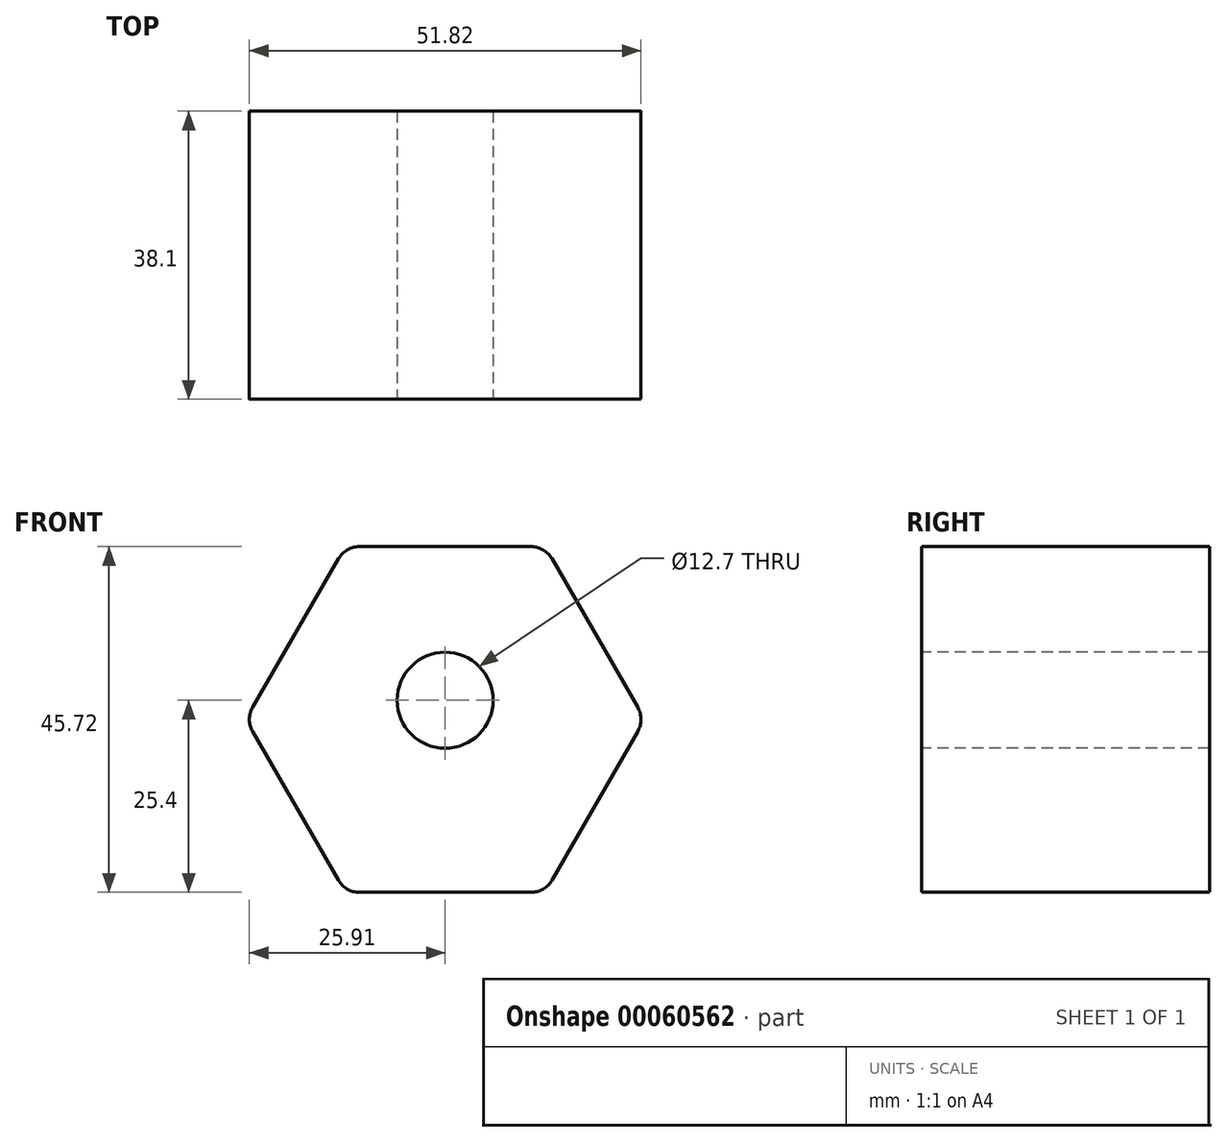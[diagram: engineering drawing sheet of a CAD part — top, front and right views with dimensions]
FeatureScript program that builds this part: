
annotation { "Feature Type Name" : "Feature", "Feature Type Description" : "" }
export const myFeature = defineFeature(function(context is Context, id is Id, definition is map)
    precondition{}
    {
        {
            var Q0;
            Q0=qCreatedBy(makeId("Front.planeOp"),FACE);
            var sketch = newSketch(context, id + "F0", { "sketchPlane" : qUnion([Q0])});
            skCircle(sketch, "E0.cCircle", {"center": v(0, 0) * mm, "radius": 22.86 * mm, "construction": true});
            skLineSegment(sketch, "E0.0", {"start": v(-13.2, 22.86) * mm, "end": v(13.2, 22.86) * mm});
            skLineSegment(sketch, "E0.1", {"start": v(13.2, 22.86) * mm, "end": v(26.4, 0) * mm});
            skLineSegment(sketch, "E0.2", {"start": v(26.4, 0) * mm, "end": v(13.2, -22.86) * mm});
            skLineSegment(sketch, "E0.3", {"start": v(13.2, -22.86) * mm, "end": v(-13.2, -22.86) * mm});
            skLineSegment(sketch, "E0.4", {"start": v(-13.2, -22.86) * mm, "end": v(-26.4, 0) * mm});
            skLineSegment(sketch, "E0.5", {"start": v(-26.4, 0) * mm, "end": v(-13.2, 22.86) * mm});
            skPoint(sketch, "E0.0.midPoint", {"position": v(0, 22.86) * mm});
            skSolve(sketch);
        }
        {
            var Q0;
            Q0 = qSketchRegion(id + "F0", true);
            extrude(context, id + "F1", {"entities" : qUnion([Q0]), "depth" : 38.1 * mm});
        }
        {
            var Q0;
            Q0=makeQuery(id+"F1.opExtrude","SWEPT_EDGE",EDGE,{"disambiguationData":[OSD([sQuery(id+"F0.wireOp",EDGE,"E0.0"),sQuery(id+"F0.wireOp",EDGE,"E0.1")])]});
            var Q1;
            Q1=makeQuery(id+"F1.opExtrude","SWEPT_EDGE",EDGE,{"disambiguationData":[OSD([sQuery(id+"F0.wireOp",EDGE,"E0.1"),sQuery(id+"F0.wireOp",EDGE,"E0.2")])]});
            var Q2;
            Q2=makeQuery(id+"F1.opExtrude","SWEPT_EDGE",EDGE,{"disambiguationData":[OSD([sQuery(id+"F0.wireOp",EDGE,"E0.2"),sQuery(id+"F0.wireOp",EDGE,"E0.3")])]});
            var Q3;
            Q3=makeQuery(id+"F1.opExtrude","SWEPT_EDGE",EDGE,{"disambiguationData":[OSD([sQuery(id+"F0.wireOp",EDGE,"E0.3"),sQuery(id+"F0.wireOp",EDGE,"E0.4")])]});
            var Q4;
            Q4=makeQuery(id+"F1.opExtrude","SWEPT_EDGE",EDGE,{"disambiguationData":[OSD([sQuery(id+"F0.wireOp",EDGE,"E0.4"),sQuery(id+"F0.wireOp",EDGE,"E0.5")])]});
            var Q5;
            Q5=makeQuery(id+"F1.opExtrude","SWEPT_EDGE",EDGE,{"disambiguationData":[OSD([sQuery(id+"F0.wireOp",EDGE,"E0.0"),sQuery(id+"F0.wireOp",EDGE,"E0.5")])]});
            fillet(context, id + "F2", {"entities" : qUnion([Q0, Q1, Q2, Q3, Q4, Q5]), "radius" : 3.17 * mm, "tangentPropagation" : true, "allowEdgeOverflow" : false});
        }
        {
            var Q0;
            Q0=makeQuery(id+"F1.opExtrude","CAP_FACE",FACE,{"disambiguationData":[OSD([sQuery(id+"F0.wireOp",EDGE,"E0.0"),sQuery(id+"F0.wireOp",EDGE,"E0.1"),sQuery(id+"F0.wireOp",EDGE,"E0.2"),sQuery(id+"F0.wireOp",EDGE,"E0.3"),sQuery(id+"F0.wireOp",EDGE,"E0.4"),sQuery(id+"F0.wireOp",EDGE,"E0.5")])],"isStart":false});
            var sketch = newSketch(context, id + "F3", { "sketchPlane" : qUnion([Q0])});
            skLineSegment(sketch, "E1", {"start": v(0, 22.86) * mm, "end": v(0, 8.89) * mm});
            skLineSegment(sketch, "E2", {"start": v(0, 8.89) * mm, "end": v(0, 2.54) * mm});
            skCircle(sketch, "E3", {"center": v(0, 2.54) * mm, "radius": 6.35 * mm});
            skSolve(sketch);
        }
        {
            var Q0;
            Q0 = qSketchRegion(id + "F3", true);
            extrude(context, id + "F4", {"entities" : qUnion([Q0]), "operationType" : NewBodyOperationType.REMOVE, "endBound" : BoundingType.UP_TO_NEXT, "oppositeDirection" : true, "depth" : 25.4 * mm});
        }
    });
